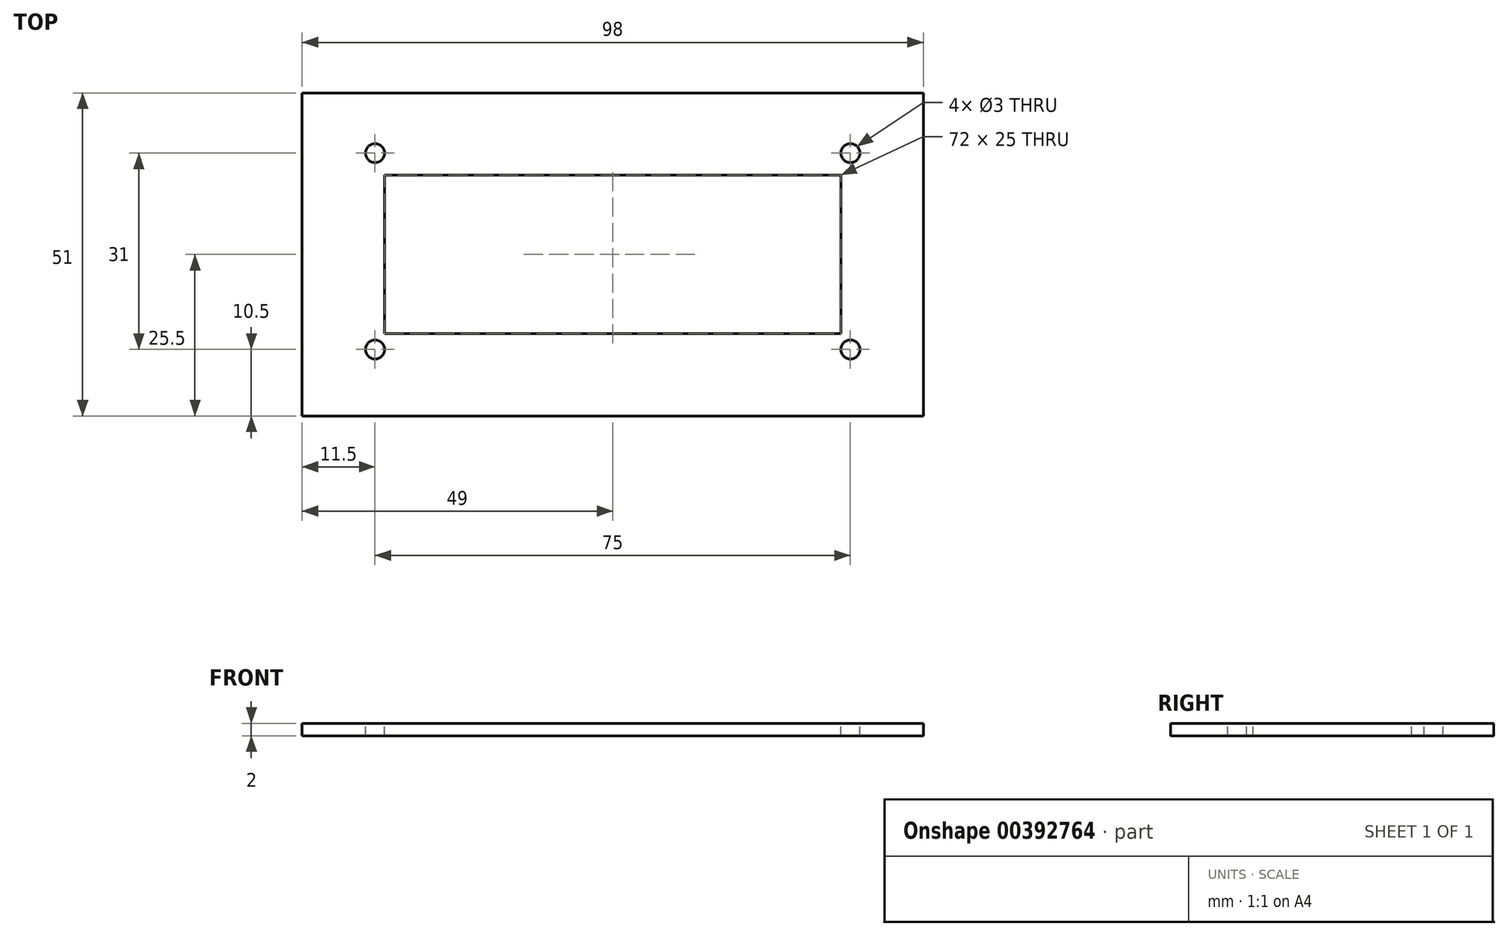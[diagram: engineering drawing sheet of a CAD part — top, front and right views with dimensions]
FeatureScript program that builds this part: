
annotation { "Feature Type Name" : "Feature", "Feature Type Description" : "" }
export const myFeature = defineFeature(function(context is Context, id is Id, definition is map)
    precondition{}
    {
        {
            var Q0;
            Q0=qCreatedBy(makeId("Top.planeOp"),FACE);
            var sketch = newSketch(context, id + "F0", { "sketchPlane" : qUnion([Q0])});
            skLineSegment(sketch, "E0.bottom", {"start": v(13, 38) * mm, "end": v(-85, 38) * mm});
            skLineSegment(sketch, "E0.top", {"start": v(13, -13) * mm, "end": v(-85, -13) * mm});
            skLineSegment(sketch, "E0.left", {"start": v(13, 38) * mm, "end": v(13, -13) * mm});
            skLineSegment(sketch, "E0.right", {"start": v(-85, 38) * mm, "end": v(-85, -13) * mm});
            skLineSegment(sketch, "E1.bottom", {"start": v(-72, 25) * mm, "end": v(0, 25) * mm});
            skLineSegment(sketch, "E1.top", {"start": v(-72, 0) * mm, "end": v(0, 0) * mm});
            skLineSegment(sketch, "E1.left", {"start": v(-72, 25) * mm, "end": v(-72, 0) * mm});
            skCircle(sketch, "E2", {"center": v(-73.5, -2.5) * mm, "radius": 1.5 * mm});
            skCircle(sketch, "E3.0.1.0", {"center": v(-73.5, 28.5) * mm, "radius": 1.5 * mm});
            skCircle(sketch, "E3.1.0.0", {"center": v(1.5, -2.5) * mm, "radius": 1.5 * mm});
            skCircle(sketch, "E3.1.1.0", {"center": v(1.5, 28.5) * mm, "radius": 1.5 * mm});
            skLineSegment(sketch, "E3.direction1", {"start": v(-73.5, -2.5) * mm, "end": v(1.5, -2.5) * mm, "construction": true});
            skLineSegment(sketch, "E3.direction2", {"start": v(-73.5, -2.5) * mm, "end": v(-73.5, 28.5) * mm, "construction": true});
            skLineSegment(sketch, "E4", {"start": v(0, 25) * mm, "end": v(0, 0) * mm});
            skSolve(sketch);
        }
        {
            var Q0;
            Q0=makeQuery(id+"F0.imprint","IMPRINT",FACE,{"disambiguationData":[TD([[makeQuery(id+"F0.imprint","IMPRINT",EDGE,{"derivedFrom":sQuery(id+"F0.wireOp",EDGE,"E0.bottom")}),1.0]])]});
            extrude(context, id + "F1", {"entities" : qUnion([Q0]), "oppositeDirection" : true, "depth" : 2 * mm});
        }
    });
